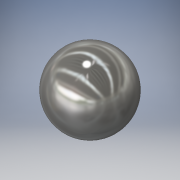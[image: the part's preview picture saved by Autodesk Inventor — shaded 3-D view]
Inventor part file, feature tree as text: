
AUTODESK INVENTOR PART (.ipt)
format: ipt  version: 2016 (Build 200138000, 138)  size: 136,704 bytes
history: native  units: in
note: dims shown in document units (in); Inventor stores cm internally (conversion verified against a paired STEP export)
features: revolve x1, sketch x1
ambient origin geometry x8: Origin, YZ Plane, XZ Plane, XY Plane, X Axis, Y Axis, Z Axis, Center Point
bodies: Solid1 (feature_tree)
feature tree (2):
  revolve  "Revolution1"  Angle=90.0deg
  sketch  "Sketch1"  dims[d0=0.687in d1=90.0deg]
